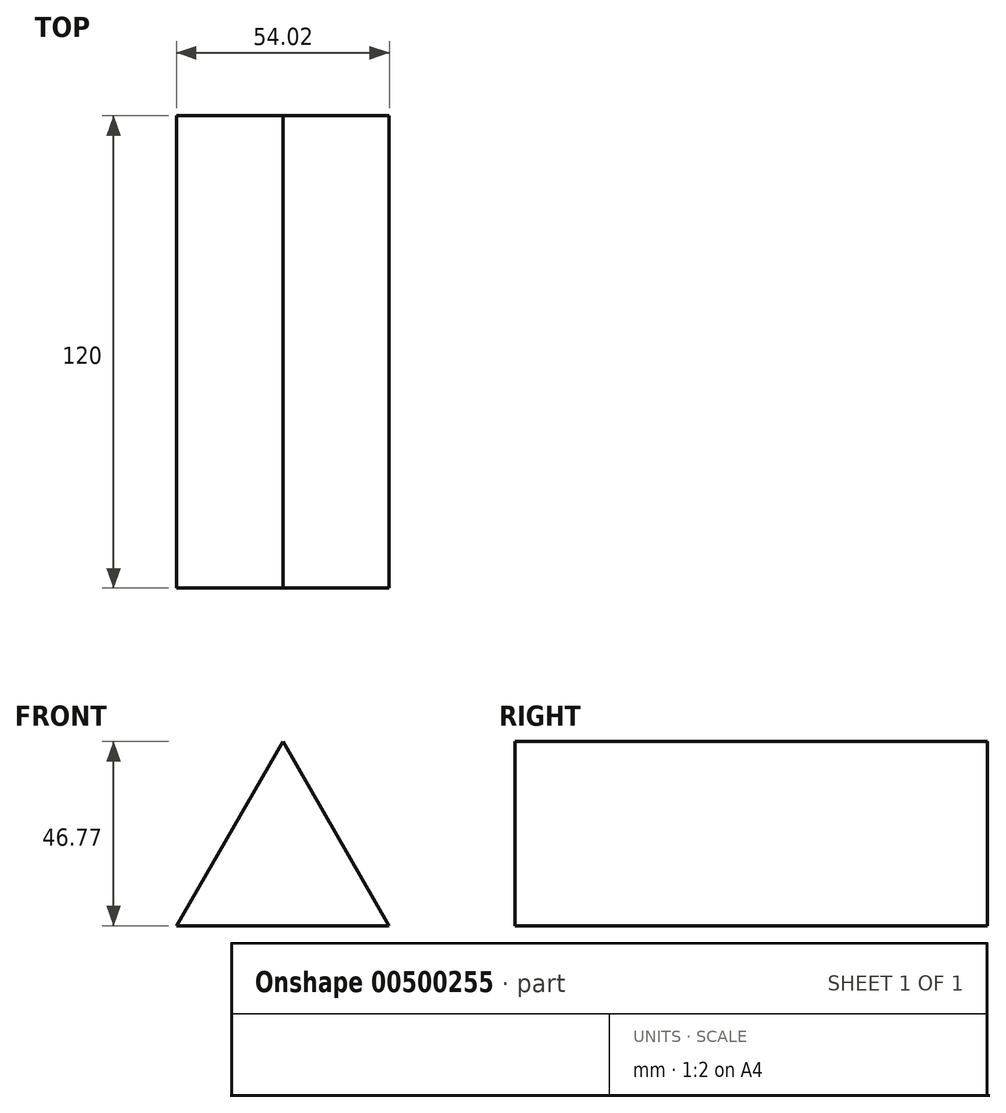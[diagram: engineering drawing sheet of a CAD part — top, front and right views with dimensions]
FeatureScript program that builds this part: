
annotation { "Feature Type Name" : "Feature", "Feature Type Description" : "" }
export const myFeature = defineFeature(function(context is Context, id is Id, definition is map)
    precondition{}
    {
        {
            var Q0;
            Q0=qCreatedBy(makeId("Front.planeOp"),FACE);
            var sketch = newSketch(context, id + "F0", { "sketchPlane" : qUnion([Q0])});
            skCircle(sketch, "E0.cCircle", {"center": v(0, 0) * mm, "radius": 31.18 * mm, "construction": true});
            skLineSegment(sketch, "E0.0", {"start": v(0, 31.18) * mm, "end": v(27, -15.6) * mm});
            skLineSegment(sketch, "E0.1", {"start": v(27, -15.6) * mm, "end": v(-27, -15.6) * mm});
            skLineSegment(sketch, "E0.2", {"start": v(-27, -15.6) * mm, "end": v(0, 31.18) * mm});
            skSolve(sketch);
        }
        {
            var Q0;
            Q0=makeQuery(id+"F0.imprint","IMPRINT",FACE,{"disambiguationData":[TD([[makeQuery(id+"F0.imprint","IMPRINT",EDGE,{"derivedFrom":sQuery(id+"F0.wireOp",EDGE,"E0.0")}),-1.0]])]});
            extrude(context, id + "F1", {"entities" : qUnion([Q0]), "depth" : 120 * mm});
        }
    });
